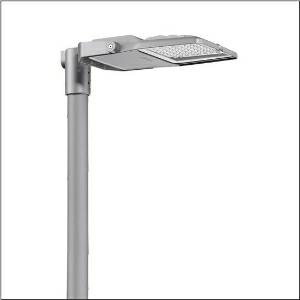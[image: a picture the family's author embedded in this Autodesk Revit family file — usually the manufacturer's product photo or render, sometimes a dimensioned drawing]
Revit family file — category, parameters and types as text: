
# Revit family: floodlight_fl_21_iq_mini___pl33t_5xa7771c4f3a_1d16
name_source: partatom
category: Lighting Fixtures
units: mm (PartAtom-declared; Revit-internal decimal feet)

## family parameters
Cut with Voids When Loaded = No
Host = Face
Light Source = No
Part Type = Normal
Room Calculation Point = No
Round Connector Dimension = Use Diameter
Shared = No

## types (1)
- --- (1 x LED, 12570 lm, 87.2 W, 4000K)
    Apparent Load = 87 VA
    CIE Flux Codes = 26 75 99 100 100
    Color Rendering = 70
    Color Temperature = 4000K
    Default Elevation = 1800 mm
    Description = Floodlight FL 21 iQ mini, floodlight, primary light control with lens, of PMMA, primary optical cover: protective disc, of toughened safety glass, transparent, light distribution: PL33T, light emission: direct distribution, installation type: surface-mounted, LED, High Power LED, rated luminous flux: 12.570lm, luminous efficacy: 144lm/W, light colour: 740, colour temperature: 4000K, control gear: iQ Comfort/DALI, control: Auto-Match, Temp-Guard, Lumen-Switch, Night-Set, Smart-Wire, Light-Fading, Desk-Remote (wireless, voltage-free reading and setting of iQ features in the workshop via application-optimized NFC function/RFID function), optimised constant luminous flux control (CLO 2.0), with terminal, 6-pole, mains connection: 220..240V, AC, 50/60Hz, start of lifetime: 87W, end of service life: 92W, reduction: 40W, luminaire housing, of diecast aluminium, powder-coated, Siteco® metallic grey (DB 702S), corrosivity category C5 mid according to DIN EN ISO 12944, suitable for swimming pools, chlorine-resistant, sealing non-destructively replaceable, please order mast flange separately, mast bracket, of steel, galvanised, powder-coated, Siteco® metallic grey (DB 702S), protection rating (complete): IP66, insulation class (complete): insulation class II (safety insulation), certification: CE, ENEC, VDE, protection symbol: D, impact resistance: IK08, permissible operating ambient temperature: -40..+40°C, permissible operating ambient temperature for outdoor applications: -40..+50°C, standard: DIN EN 12944, LABS conformity tested according to VDMA 24364:2018-05, packaging unit: 1 piece

Light Distribution: PL33T
    Height = 70 mm
    Lamp = 1 x LED
    Lamp Light Flux = 12570 lm
    Lamp Power = 87.2 W
    Lamp count = 1
    Length = 485 mm
    Luminous efficacy = 144 lm/W
    Manufacturer = Siteco
    ModVariant = No
    Model = 5XA7771C4F3A
    Number of Poles = 1
    OnlyDefault = Yes
    Power Factor = 1
    Product Name = Floodlight FL 21 iQ mini | PL33T
    Product group = floodlight | pylon annexe
    ProductGroupID = 6200
    Protection Class = Protection class II
    Protection Degree = IP 66
    RLX_Detail_Level = 1
    RLX_Emergency_Light_Flux = 0 lm
    RLX_Emergency_Type = 0
    RLX_Emergency_Type_DB = No
    RlxData = <blob elided: 101281 chars, md5=f4f0cb59>
    Socket = socket
    Standby Power = 0 W
    System Light Flux = 12570 lm
    System Power = 87 W
    Type Comments = factory setting: luminous flux: 100 % | dim-lin: 254 | 456 mA
    Type Image = l_1007125.jpg
    URL = http://relux.com
    VarID = @adj_149636
    Voltage = 0 V
    Weight = 0.00 kg
    Width = 337 mm

## geometry (parser evidence)
native form markers: Blend x4, Sweep x11
no freeform markers — native parametric forms only
